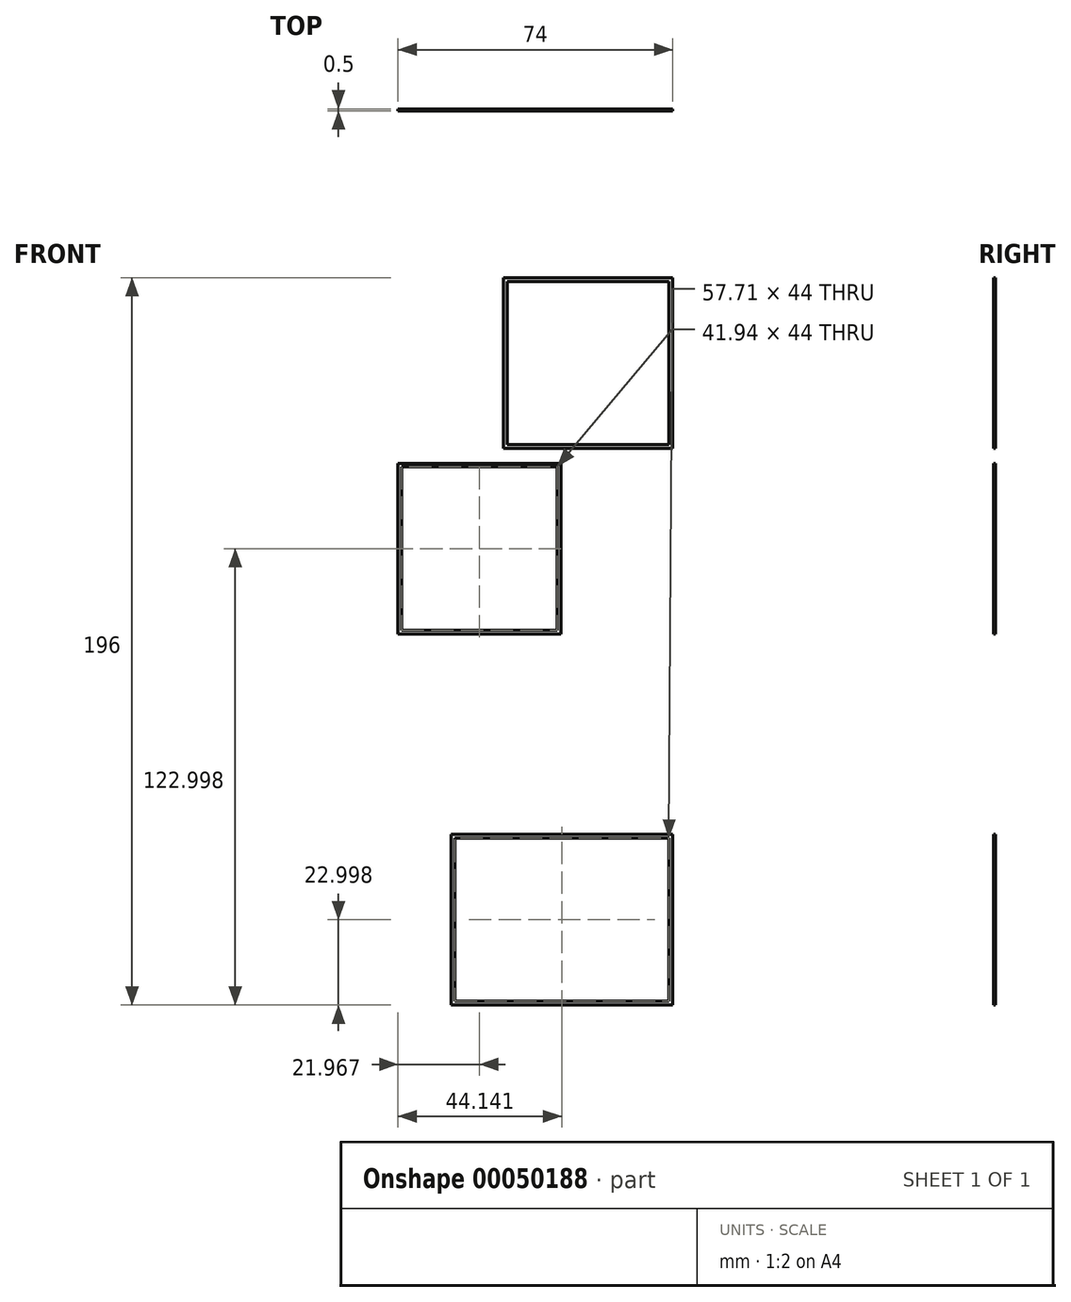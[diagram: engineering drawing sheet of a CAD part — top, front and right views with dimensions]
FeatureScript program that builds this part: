
annotation { "Feature Type Name" : "Feature", "Feature Type Description" : "" }
export const myFeature = defineFeature(function(context is Context, id is Id, definition is map)
    precondition{}
    {
        {
            var Q0;
            Q0=qCreatedBy(makeId("Front.planeOp"),FACE);
            var sketch = newSketch(context, id + "F0", { "sketchPlane" : qUnion([Q0])});
            skLineSegment(sketch, "E0.bottom", {"start": v(-59.74, 128.88) * mm, "end": v(20.26, 128.88) * mm});
            skLineSegment(sketch, "E0.top", {"start": v(-59.74, -73.12) * mm, "end": v(20.26, -73.12) * mm});
            skLineSegment(sketch, "E0.left", {"start": v(-59.74, 128.88) * mm, "end": v(-59.74, -73.12) * mm});
            skLineSegment(sketch, "E0.right", {"start": v(20.26, 128.88) * mm, "end": v(20.26, -73.12) * mm});
            skSolve(sketch);
        }
        {
            var Q0;
            Q0=qSketchRegion(id+"F0",true);
            extrude(context, id + "F1", {"entities" : qUnion([Q0]), "depth" : 3 * mm});
        }
        {
            var Q0;
            Q0=makeQuery(id+"F1.opExtrude","CAP_FACE",FACE,{"disambiguationData":[OSD([sQuery(id+"F0.wireOp",EDGE,"E0.bottom"),sQuery(id+"F0.wireOp",EDGE,"E0.top"),sQuery(id+"F0.wireOp",EDGE,"E0.left"),sQuery(id+"F0.wireOp",EDGE,"E0.right")])],"isStart":false});
            var sketch = newSketch(context, id + "F2", { "sketchPlane" : qUnion([Q0])});
            skLineSegment(sketch, "E1.bottom", {"start": v(-59.74, 128.88) * mm, "end": v(20.26, 128.88) * mm});
            skLineSegment(sketch, "E1.top", {"start": v(-59.74, -73.12) * mm, "end": v(20.26, -73.12) * mm});
            skLineSegment(sketch, "E1.left", {"start": v(-59.74, 128.88) * mm, "end": v(-59.74, -73.12) * mm});
            skLineSegment(sketch, "E1.right", {"start": v(20.26, 128.88) * mm, "end": v(20.26, -73.12) * mm});
            skLineSegment(sketch, "E2.0", {"start": v(-57.74, 126.88) * mm, "end": v(18.26, 126.88) * mm});
            skLineSegment(sketch, "E2.1", {"start": v(-57.74, 126.88) * mm, "end": v(-57.74, -71.12) * mm});
            skLineSegment(sketch, "E2.2", {"start": v(-57.74, -71.12) * mm, "end": v(18.26, -71.12) * mm});
            skLineSegment(sketch, "E2.3", {"start": v(18.26, 126.88) * mm, "end": v(18.26, -71.12) * mm});
            skPoint(sketch, "E3.start.orphan", {"position": v(-19.74, -71.12) * mm});
            skLineSegment(sketch, "E4.top", {"start": v(18.26, -71.12) * mm, "end": v(-43.45, -71.12) * mm});
            skLineSegment(sketch, "E4.left", {"start": v(18.26, -23.12) * mm, "end": v(18.26, -71.12) * mm});
            skLineSegment(sketch, "E5.right", {"start": v(-57.74, 28.88) * mm, "end": v(-57.74, 76.88) * mm});
            skLineSegment(sketch, "E6", {"start": v(-43.45, -42.18) * mm, "end": v(-41.45, -42.18) * mm});
            skLineSegment(sketch, "E7.bottom", {"start": v(-41.45, -25.12) * mm, "end": v(16.26, -25.12) * mm});
            skLineSegment(sketch, "E7.top", {"start": v(-41.45, -69.12) * mm, "end": v(16.26, -69.12) * mm});
            skLineSegment(sketch, "E7.left", {"start": v(-41.45, -25.12) * mm, "end": v(-41.45, -69.12) * mm});
            skLineSegment(sketch, "E7.right", {"start": v(16.26, -25.12) * mm, "end": v(16.26, -69.12) * mm});
            skPoint(sketch, "E8.end.orphan", {"position": v(-12.6, -69.12) * mm});
            skPoint(sketch, "E8.start.orphan", {"position": v(-12.6, -71.12) * mm});
            skPoint(sketch, "E9.end.orphan", {"position": v(16.26, -42.68) * mm});
            skPoint(sketch, "E10.end.orphan", {"position": v(-19.74, -25.12) * mm});
            skPoint(sketch, "E11.start.orphan", {"position": v(-19.74, -23.12) * mm});
            skLineSegment(sketch, "E12.bottom", {"start": v(-55.74, 74.88) * mm, "end": v(-13.8, 74.88) * mm});
            skLineSegment(sketch, "E12.top", {"start": v(-55.74, 30.88) * mm, "end": v(-13.8, 30.88) * mm});
            skLineSegment(sketch, "E12.left", {"start": v(-55.74, 74.88) * mm, "end": v(-55.74, 30.88) * mm});
            skLineSegment(sketch, "E12.right", {"start": v(-13.8, 74.88) * mm, "end": v(-13.8, 30.88) * mm});
            skPoint(sketch, "E13.orphan", {"position": v(-11.8, 28.88) * mm});
            skPoint(sketch, "E14.end.orphan", {"position": v(-38.4, 30.88) * mm});
            skPoint(sketch, "E15.end.orphan", {"position": v(-55.74, 55.9) * mm});
            skPoint(sketch, "E16.end.orphan", {"position": v(-13.8, 51.95) * mm});
            skPoint(sketch, "E17.end.orphan", {"position": v(-19.74, 28.88) * mm});
            skPoint(sketch, "E18.end.orphan", {"position": v(-19.74, 74.88) * mm});
            skPoint(sketch, "E19.end.orphan", {"position": v(-19.74, 78.88) * mm});
            skPoint(sketch, "E19.start.orphan", {"position": v(-19.74, 76.88) * mm});
            skLineSegment(sketch, "E20.bottom", {"start": v(-27.37, 124.88) * mm, "end": v(16.26, 124.88) * mm});
            skLineSegment(sketch, "E20.top", {"start": v(-27.37, 80.88) * mm, "end": v(16.26, 80.88) * mm});
            skLineSegment(sketch, "E20.left", {"start": v(-27.37, 124.88) * mm, "end": v(-27.37, 80.88) * mm});
            skLineSegment(sketch, "E20.right", {"start": v(16.26, 124.88) * mm, "end": v(16.26, 80.88) * mm});
            skPoint(sketch, "E21.end.orphan", {"position": v(-3.38, 124.88) * mm});
            skPoint(sketch, "E22.end.orphan", {"position": v(16.26, 107.55) * mm});
            skPoint(sketch, "E23.end.orphan", {"position": v(-6.54, 80.88) * mm});
            skPoint(sketch, "E24.right.end.orphan", {"position": v(-29.37, 78.88) * mm});
            skPoint(sketch, "E25.end.orphan", {"position": v(-27.37, 103.86) * mm});
            skSolve(sketch);
        }
        {
            var Q0;
            Q0=makeQuery(id+"F2.imprint","IMPRINT",FACE,{"disambiguationData":[TD([[makeQuery(id+"F2.imprint","IMPRINT",EDGE,{"derivedFrom":sQuery(id+"F2.wireOp",EDGE,"E12.bottom")}),-1.0]])]});
            var Q1;
            Q1=makeQuery(id+"F2.imprint","IMPRINT",FACE,{"disambiguationData":[TD([[makeQuery(id+"F2.imprint","IMPRINT",EDGE,{"derivedFrom":sQuery(id+"F2.wireOp",EDGE,"E20.bottom")}),-1.0]])]});
            var Q2;
            {var subQ3=sQuery(id+"F2.wireOp",EDGE,"E7.bottom");Q2=makeQuery(id+"F2.imprint","IMPRINT",FACE,{"disambiguationData":[TD([[makeQuery(id+"F2.imprint","IMPRINT",EDGE,{"derivedFrom":subQ3}),-1.0]])]});}
            extrude(context, id + "F3", {"entities" : qUnion([Q0, Q1, Q2]), "operationType" : NewBodyOperationType.REMOVE, "oppositeDirection" : true, "depth" : 25 * mm});
        }
        {
            var Q0;
            Q0=makeQuery(id+"F1.opExtrude","CAP_FACE",FACE,{"disambiguationData":[OSD([sQuery(id+"F0.wireOp",EDGE,"E0.bottom"),sQuery(id+"F0.wireOp",EDGE,"E0.top"),sQuery(id+"F0.wireOp",EDGE,"E0.left"),sQuery(id+"F0.wireOp",EDGE,"E0.right")])],"isStart":true});
            var sketch = newSketch(context, id + "F4", { "sketchPlane" : qUnion([Q0])});
            skSolve(sketch);
        }
        {
            var Q0;
            {var subQ3=sQuery(id+"F0.wireOp",EDGE,"E0.bottom");Q0=makeQuery(id+"F4.imprint","IMPRINT",FACE,{"disambiguationData":[TD([[makeQuery(id+"F4.imprint","IMPRINT",EDGE,{"derivedFrom":makeQuery(id+"F1.opExtrude","CAP_EDGE",EDGE,{"disambiguationData":[OSD([subQ3])],"isStart":true})}),1.0]])]});}
            var sketch = newSketch(context, id + "F5", { "sketchPlane" : qUnion([Q0])});
            skLineSegment(sketch, "E26.0", {"start": v(27.37, 124.88) * mm, "end": v(-16.26, 124.88) * mm});
            skLineSegment(sketch, "E27.0", {"start": v(-16.26, 124.88) * mm, "end": v(-16.26, 80.88) * mm});
            skLineSegment(sketch, "E28.0", {"start": v(27.37, 124.88) * mm, "end": v(27.37, 80.88) * mm});
            skLineSegment(sketch, "E29.0", {"start": v(27.37, 80.88) * mm, "end": v(-16.26, 80.88) * mm});
            skLineSegment(sketch, "E30.0", {"start": v(55.74, 74.88) * mm, "end": v(13.8, 74.88) * mm});
            skLineSegment(sketch, "E31.0", {"start": v(13.8, 74.88) * mm, "end": v(13.8, 30.88) * mm});
            skLineSegment(sketch, "E32.0", {"start": v(55.74, 74.88) * mm, "end": v(55.74, 30.88) * mm});
            skLineSegment(sketch, "E33.0", {"start": v(55.74, 30.88) * mm, "end": v(13.8, 30.88) * mm});
            skLineSegment(sketch, "E34.0", {"start": v(41.45, -25.12) * mm, "end": v(-16.26, -25.12) * mm});
            skLineSegment(sketch, "E35.0", {"start": v(41.45, -25.12) * mm, "end": v(41.45, -69.12) * mm});
            skLineSegment(sketch, "E36.0", {"start": v(-16.26, -25.12) * mm, "end": v(-16.26, -69.12) * mm});
            skLineSegment(sketch, "E37.0", {"start": v(41.45, -69.12) * mm, "end": v(-16.26, -69.12) * mm});
            skLineSegment(sketch, "E38.0", {"start": v(42.45, -24.12) * mm, "end": v(-17.26, -24.12) * mm});
            skLineSegment(sketch, "E38.1", {"start": v(42.45, -24.12) * mm, "end": v(42.45, -70.12) * mm});
            skLineSegment(sketch, "E38.2", {"start": v(42.45, -70.12) * mm, "end": v(-17.26, -70.12) * mm});
            skLineSegment(sketch, "E38.3", {"start": v(-17.26, -24.12) * mm, "end": v(-17.26, -70.12) * mm});
            skLineSegment(sketch, "E39.0", {"start": v(56.74, 75.88) * mm, "end": v(12.8, 75.88) * mm});
            skLineSegment(sketch, "E39.1", {"start": v(56.74, 75.88) * mm, "end": v(56.74, 29.88) * mm});
            skLineSegment(sketch, "E39.2", {"start": v(56.74, 29.88) * mm, "end": v(12.8, 29.88) * mm});
            skLineSegment(sketch, "E39.3", {"start": v(12.8, 75.88) * mm, "end": v(12.8, 29.88) * mm});
            skLineSegment(sketch, "E40.0", {"start": v(28.37, 125.88) * mm, "end": v(-17.26, 125.88) * mm});
            skLineSegment(sketch, "E40.1", {"start": v(28.37, 125.88) * mm, "end": v(28.37, 79.88) * mm});
            skLineSegment(sketch, "E40.2", {"start": v(28.37, 79.88) * mm, "end": v(-17.26, 79.88) * mm});
            skLineSegment(sketch, "E40.3", {"start": v(-17.26, 125.88) * mm, "end": v(-17.26, 79.88) * mm});
            skSolve(sketch);
        }
        {
            var Q0;
            Q0 = qSketchRegion(id + "F5", true);
            extrude(context, id + "F6", {"entities" : qUnion([Q0]), "operationType" : NewBodyOperationType.ADD, "depth" : 0.5 * mm});
        }
        {
            var Q0;
            Q0=makeQuery(id+"F1.opExtrude","CAP_FACE",FACE,{"disambiguationData":[OSD([sQuery(id+"F0.wireOp",EDGE,"E0.bottom"),sQuery(id+"F0.wireOp",EDGE,"E0.top"),sQuery(id+"F0.wireOp",EDGE,"E0.left"),sQuery(id+"F0.wireOp",EDGE,"E0.right")])],"isStart":false});
            var sketch = newSketch(context, id + "F7", { "sketchPlane" : qUnion([Q0])});
            skLineSegment(sketch, "E41.bottom", {"start": v(-73.5, 138.72) * mm, "end": v(35.83, 138.72) * mm});
            skLineSegment(sketch, "E41.top", {"start": v(-73.5, -86.18) * mm, "end": v(35.83, -86.18) * mm});
            skLineSegment(sketch, "E41.left", {"start": v(-73.5, 138.72) * mm, "end": v(-73.5, -86.18) * mm});
            skLineSegment(sketch, "E41.right", {"start": v(35.83, 138.72) * mm, "end": v(35.83, -86.18) * mm});
            skSolve(sketch);
        }
        {
            var Q0;
            Q0 = qSketchRegion(id + "F7", true);
            extrude(context, id + "F8", {"entities" : qUnion([Q0]), "operationType" : NewBodyOperationType.REMOVE, "oppositeDirection" : true, "depth" : 3 * mm});
        }
    });
